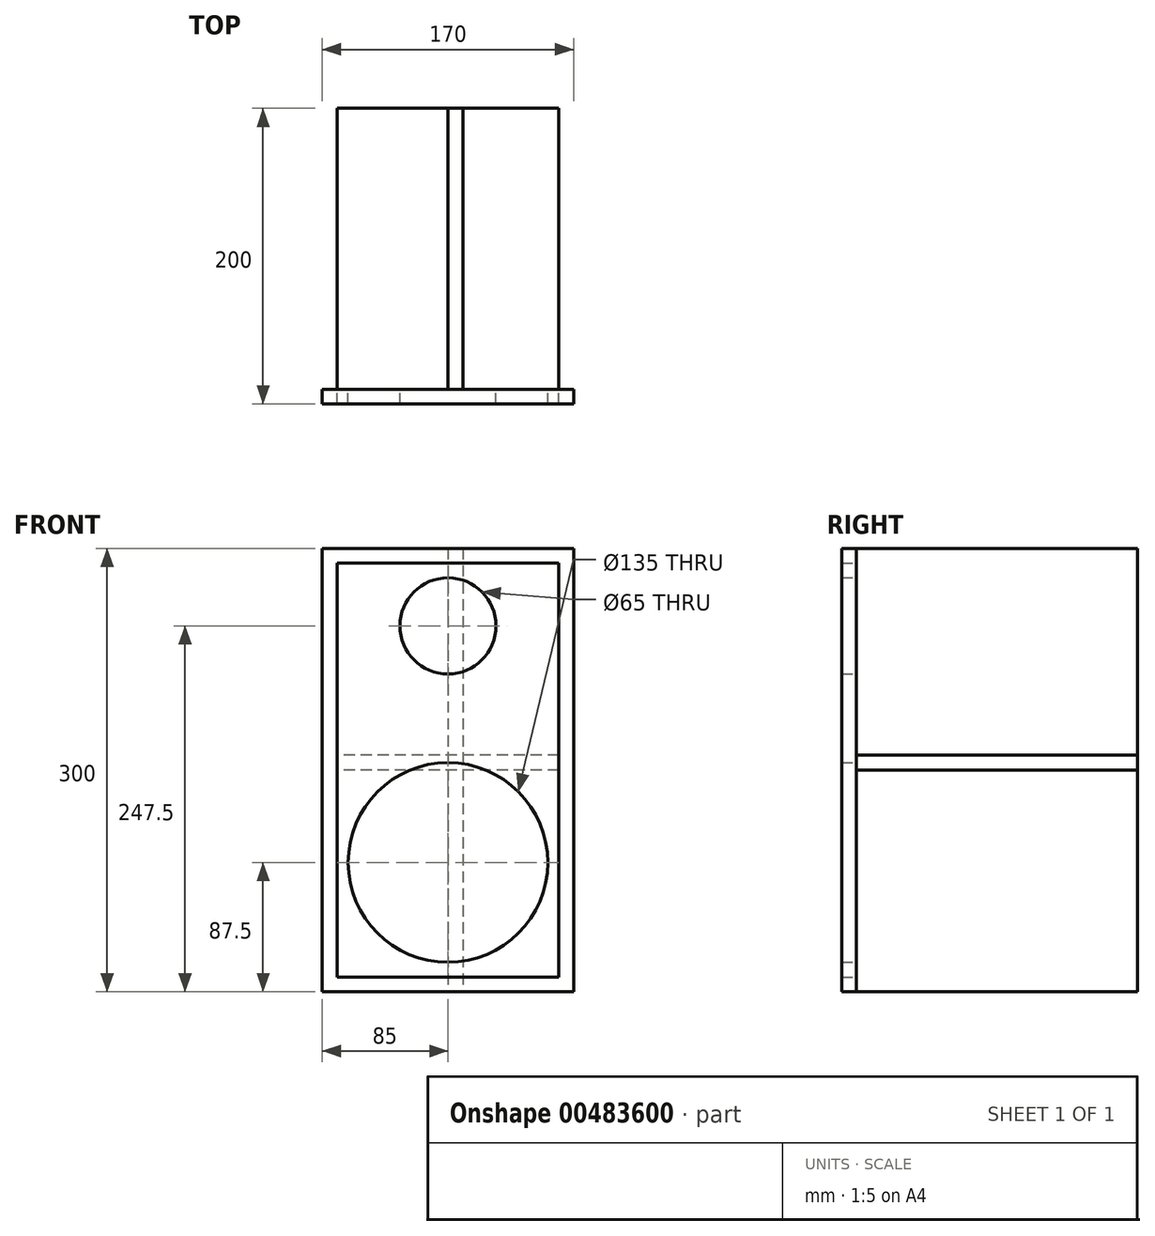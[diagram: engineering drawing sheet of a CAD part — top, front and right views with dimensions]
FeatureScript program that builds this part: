
annotation { "Feature Type Name" : "Feature", "Feature Type Description" : "" }
export const myFeature = defineFeature(function(context is Context, id is Id, definition is map)
    precondition{}
    {
        {
            assignVariable(context, id + "F0", {"name" : "thickness", "anyValue" : 10});
        }
        {
            var Q0;
            Q0=qCreatedBy(makeId("Front.planeOp"),FACE);
            var sketch = newSketch(context, id + "F1", { "sketchPlane" : qUnion([Q0])});
            skLineSegment(sketch, "E0.bottom", {"start": v(85, -150) * mm, "end": v(-85, -150) * mm});
            skLineSegment(sketch, "E0.top", {"start": v(85, 150) * mm, "end": v(-85, 150) * mm});
            skLineSegment(sketch, "E0.left", {"start": v(85, -150) * mm, "end": v(85, 150) * mm});
            skLineSegment(sketch, "E0.right", {"start": v(-85, -150) * mm, "end": v(-85, 150) * mm});
            skPoint(sketch, "E0.middle", {"position": v(0, 0) * mm});
            skLineSegment(sketch, "E1", {"start": v(0, -150) * mm, "end": v(0, 150) * mm, "construction": true});
            skCircle(sketch, "E2", {"center": v(0, -62.5) * mm, "radius": 67.5 * mm});
            skCircle(sketch, "E3", {"center": v(0, 97.5) * mm, "radius": 32.5 * mm});
            skSolve(sketch);
        }
        {
            var Q0;
            Q0=makeQuery(id+"F1.imprint","IMPRINT",FACE,{"disambiguationData":[TD([[makeQuery(id+"F1.imprint","IMPRINT",EDGE,{"derivedFrom":sQuery(id+"F1.wireOp",EDGE,"E0.bottom")}),-1.0]])]});
            extrude(context, id + "F2", {"entities" : qUnion([Q0]), "depth" : (getVariable(context, 'thickness')) * mm});
        }
        {
            var Q0;
            Q0=qCreatedBy(makeId("Top.planeOp"),FACE);
            var sketch = newSketch(context, id + "F3", { "sketchPlane" : qUnion([Q0])});
            skLineSegment(sketch, "E4.bottom", {"start": v(75, 0) * mm, "end": v(-75, 0) * mm});
            skLineSegment(sketch, "E4.top", {"start": v(75, 190) * mm, "end": v(-75, 190) * mm});
            skLineSegment(sketch, "E4.left", {"start": v(75, 0) * mm, "end": v(75, 190) * mm});
            skLineSegment(sketch, "E4.right", {"start": v(-75, 0) * mm, "end": v(-75, 190) * mm});
            skSolve(sketch);
        }
        {
            var Q0;
            Q0=makeQuery(id+"F3.imprint","IMPRINT",FACE,{"disambiguationData":[TD([[makeQuery(id+"F3.imprint","IMPRINT",EDGE,{"derivedFrom":sQuery(id+"F3.wireOp",EDGE,"E4.bottom")}),-1.0]])]});
            extrude(context, id + "F4", {"entities" : qUnion([Q0]), "depth" : (getVariable(context, 'thickness')) * mm});
        }
        {
            var Q0;
            Q0=qCreatedBy(makeId("Right.planeOp"),FACE);
            var sketch = newSketch(context, id + "F5", { "sketchPlane" : qUnion([Q0])});
            skLineSegment(sketch, "E5.bottom", {"start": v(0, 150) * mm, "end": v(190, 150) * mm});
            skLineSegment(sketch, "E5.top", {"start": v(0, -150) * mm, "end": v(190, -150) * mm});
            skLineSegment(sketch, "E5.left", {"start": v(0, 150) * mm, "end": v(0, -150) * mm});
            skLineSegment(sketch, "E5.right", {"start": v(190, 150) * mm, "end": v(190, -150) * mm});
            skSolve(sketch);
        }
        {
            var Q0;
            Q0=makeQuery(id+"F5.imprint","IMPRINT",FACE,{"disambiguationData":[TD([[makeQuery(id+"F5.imprint","IMPRINT",EDGE,{"derivedFrom":sQuery(id+"F5.wireOp",EDGE,"E5.bottom")}),-1.0]])]});
            extrude(context, id + "F6", {"entities" : qUnion([Q0]), "depth" : (getVariable(context, 'thickness')) * mm});
        }
        {
            var Q0;
            Q0=qCreatedBy(makeId("Front.planeOp"),FACE);
            var sketch = newSketch(context, id + "F7", { "sketchPlane" : qUnion([Q0])});
            skLineSegment(sketch, "E6.bottom", {"start": v(-75, -140) * mm, "end": v(75, -140) * mm});
            skLineSegment(sketch, "E6.top", {"start": v(-75, 140) * mm, "end": v(75, 140) * mm});
            skLineSegment(sketch, "E6.left", {"start": v(-75, -140) * mm, "end": v(-75, 140) * mm});
            skLineSegment(sketch, "E6.right", {"start": v(75, -140) * mm, "end": v(75, 140) * mm});
            skPoint(sketch, "E6.middle", {"position": v(0, 0) * mm});
            skSolve(sketch);
        }
        {
            var Q0;
            Q0=makeQuery(id+"F7.imprint","IMPRINT",FACE,{"disambiguationData":[TD([[makeQuery(id+"F7.imprint","IMPRINT",EDGE,{"derivedFrom":sQuery(id+"F7.wireOp",EDGE,"E6.bottom")}),1.0]])]});
            extrude(context, id + "F8", {"entities" : qUnion([Q0]), "depth" : (getVariable(context, 'thickness')) * mm});
        }
    });
